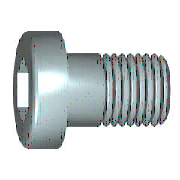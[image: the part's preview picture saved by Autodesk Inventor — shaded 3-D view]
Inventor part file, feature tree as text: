
AUTODESK INVENTOR PART (.ipt)
format: ipt  version: 2024 (Build 280153000, 153)  size: 191,488 bytes
history: native  units: mm (DEFAULTED — no unit token found)
features: other x3, extrude x1, plane x1
ambient origin geometry x7: Origin, YZ Plane, XY Plane, X Axis, Y Axis, Z Axis, Center Point
bodies: Solid1 (feature_tree)
feature tree (5):
  other  "Базовый элемент"
  other  "Фаска2"
  extrude  "Паз"  Depth=2.8mm
  other  "Work Axis1"
  plane  "Work Plane1"
